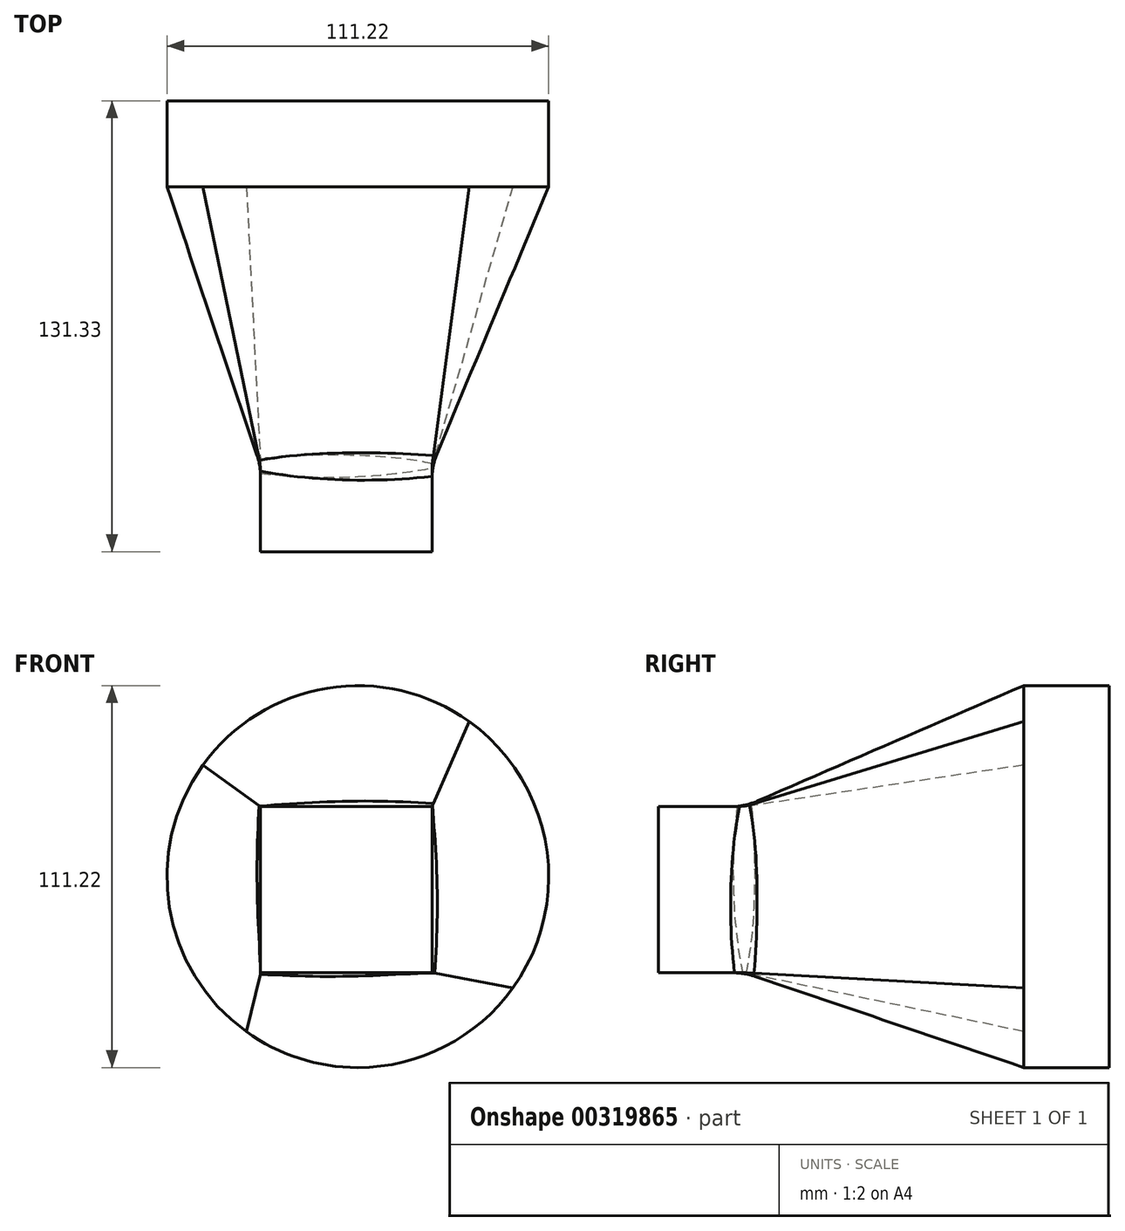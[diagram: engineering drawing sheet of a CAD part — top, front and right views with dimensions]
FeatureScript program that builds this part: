
annotation { "Feature Type Name" : "Feature", "Feature Type Description" : "" }
export const myFeature = defineFeature(function(context is Context, id is Id, definition is map)
    precondition{}
    {
        {
            var Q0;
            Q0=qCreatedBy(makeId("Front.planeOp"),FACE);
            var sketch = newSketch(context, id + "F0", { "sketchPlane" : qUnion([Q0])});
            skCircle(sketch, "E0", {"center": v(0, 0) * mm, "radius": 55.6 * mm});
            skLineSegment(sketch, "E1.bottom", {"start": v(-28.32, 20.35) * mm, "end": v(21.6, 20.35) * mm});
            skLineSegment(sketch, "E1.top", {"start": v(-28.32, -28) * mm, "end": v(21.6, -28) * mm});
            skLineSegment(sketch, "E1.left", {"start": v(-28.32, 20.35) * mm, "end": v(-28.32, -28) * mm});
            skLineSegment(sketch, "E1.right", {"start": v(21.6, 20.35) * mm, "end": v(21.6, -28) * mm});
            skSolve(sketch);
        }
        {
            var Q0;
            Q0=makeQuery(id+"F0.imprint","IMPRINT",FACE,{"disambiguationData":[TD([[makeQuery(id+"F0.imprint","IMPRINT",EDGE,{"derivedFrom":sQuery(id+"F0.wireOp",EDGE,"E1.bottom")}),-1.0]])]});
            extrude(context, id + "F1", {"entities" : qUnion([Q0]), "depth" : 25 * mm});
        }
        {
            var Q0;
            Q0=makeQuery(id+"F0.imprint","IMPRINT",FACE,{"disambiguationData":[TD([[makeQuery(id+"F0.imprint","IMPRINT",EDGE,{"derivedFrom":sQuery(id+"F0.wireOp",EDGE,"E0")}),1.0]])]});
            var Q1;
            Q1=makeQuery(id+"F0.imprint","IMPRINT",FACE,{"disambiguationData":[TD([[makeQuery(id+"F0.imprint","IMPRINT",EDGE,{"derivedFrom":sQuery(id+"F0.wireOp",EDGE,"E1.bottom")}),-1.0]])]});
            extrude(context, id + "F2", {"entities" : qUnion([Q0, Q1]), "oppositeDirection" : true, "depth" : 25 * mm});
        }
        {
            var Q0;
            Q0=makeQuery(id+"F1.opExtrude","SWEPT_BODY",BODY,{"disambiguationData":[OSD([sQuery(id+"F0.wireOp",EDGE,"E1.bottom"),sQuery(id+"F0.wireOp",EDGE,"E1.top"),sQuery(id+"F0.wireOp",EDGE,"E1.left"),sQuery(id+"F0.wireOp",EDGE,"E1.right")])]});
            transform(context, id + "F3", {"entities" : qUnion([Q0]), "transformType" : TransformType.TRANSLATION_3D, "dx" : 0 * mm, "dy" : -81.33 * mm, "dz" : 0 * mm, "makeCopy" : false});
        }
        {
            var Q1;
            Q1=makeQuery(id+"F2.opExtrude","CAP_FACE",FACE,{"disambiguationData":[OSD([sQuery(id+"F0.wireOp",EDGE,"E0")])],"isStart":true});
            var Q2;
            Q2=makeQuery(id+"F1.opExtrude","CAP_FACE",FACE,{"disambiguationData":[OSD([sQuery(id+"F0.wireOp",EDGE,"E1.bottom"),sQuery(id+"F0.wireOp",EDGE,"E1.top"),sQuery(id+"F0.wireOp",EDGE,"E1.left"),sQuery(id+"F0.wireOp",EDGE,"E1.right")])],"isStart":true});
            loft(context, id + "F4", {"operationType" : NewBodyOperationType.ADD, "sheetProfilesArray" : [{ "sheetProfileEntities" : qUnion([Q1]) }, { "sheetProfileEntities" : qUnion([Q2]) }]});
        }
        {
            var Q0;
            {var subQ0=sQuery(id+"F0.wireOp",EDGE,"E1.left");Q0=makeQuery(id+"F4.boolean.opBoolean","MERGE",EDGE,{"derivedFrom":[makeQuery(id+"F1.opExtrude","CAP_EDGE",EDGE,{"disambiguationData":[OSD([subQ0])],"isStart":true}),makeQuery(id+"F4.opLoft","MID_CAP_EDGE",EDGE,{"disambiguationData":[OSD([sQuery(id+"F0.wireOp",EDGE,"E1.bottom"),sQuery(id+"F0.wireOp",EDGE,"E1.top"),subQ0])],"capPos":1.0})]});}
            var Q1;
            {var subQ0=sQuery(id+"F0.wireOp",EDGE,"E1.right");Q1=makeQuery(id+"F4.boolean.opBoolean","MERGE",EDGE,{"derivedFrom":[makeQuery(id+"F1.opExtrude","CAP_EDGE",EDGE,{"disambiguationData":[OSD([subQ0])],"isStart":true}),makeQuery(id+"F4.opLoft","MID_CAP_EDGE",EDGE,{"disambiguationData":[OSD([sQuery(id+"F0.wireOp",EDGE,"E1.bottom"),sQuery(id+"F0.wireOp",EDGE,"E1.top"),subQ0])],"capPos":1.0})]});}
            var Q2;
            {var subQ0=sQuery(id+"F0.wireOp",EDGE,"E1.bottom");Q2=makeQuery(id+"F4.boolean.opBoolean","MERGE",EDGE,{"derivedFrom":[makeQuery(id+"F1.opExtrude","CAP_EDGE",EDGE,{"disambiguationData":[OSD([subQ0])],"isStart":true}),makeQuery(id+"F4.opLoft","MID_CAP_EDGE",EDGE,{"disambiguationData":[OSD([subQ0,sQuery(id+"F0.wireOp",EDGE,"E1.left"),sQuery(id+"F0.wireOp",EDGE,"E1.right")])],"capPos":1.0})]});}
            var Q3;
            {var subQ0=sQuery(id+"F0.wireOp",EDGE,"E1.top");Q3=makeQuery(id+"F4.boolean.opBoolean","MERGE",EDGE,{"derivedFrom":[makeQuery(id+"F1.opExtrude","CAP_EDGE",EDGE,{"disambiguationData":[OSD([subQ0])],"isStart":true}),makeQuery(id+"F4.opLoft","MID_CAP_EDGE",EDGE,{"disambiguationData":[OSD([subQ0,sQuery(id+"F0.wireOp",EDGE,"E1.left"),sQuery(id+"F0.wireOp",EDGE,"E1.right")])],"capPos":1.0})]});}
            fillet(context, id + "F5", {"entities" : qUnion([Q0, Q1, Q2, Q3]), "radius" : 20 * mm, "tangentPropagation" : true, "allowEdgeOverflow" : false});
        }
    });
